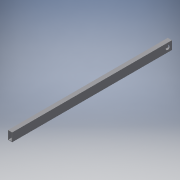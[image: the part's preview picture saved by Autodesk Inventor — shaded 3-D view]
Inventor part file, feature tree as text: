
AUTODESK INVENTOR PART (.ipt)
format: ipt  version: 2018 (Build 220112000, 112)  size: 116,224 bytes
history: native  units: in
note: dims shown in document units (in); Inventor stores cm internally (conversion verified against a paired STEP export)
features: extrude x3, sketch x3
ambient origin geometry x8: Origin, YZ Plane, XZ Plane, XY Plane, X Axis, Y Axis, Z Axis, Center Point
bodies: Solid1 (feature_tree)
feature tree (6):
  extrude  "Extrusion1"  Depth=2.0in
  extrude  "Extrusion2"  Depth=38.0in TaperAngle=0.0deg
  extrude  "Extrusion3"  Depth=1.0in TaperAngle=0.0deg
  sketch  "Sketch1"  dims[d0=1.0in d1=2.0in]
  sketch  "Sketch2"  dims[d2=0.125in d3=38.0in d4=0.0in]
  sketch  "Sketch3"  dims[d5=1.0in d7=10.0in d8=0.0in d9=1.0in d10=1.0in d11=1.125in d12=1.0in d13=0.0in]
